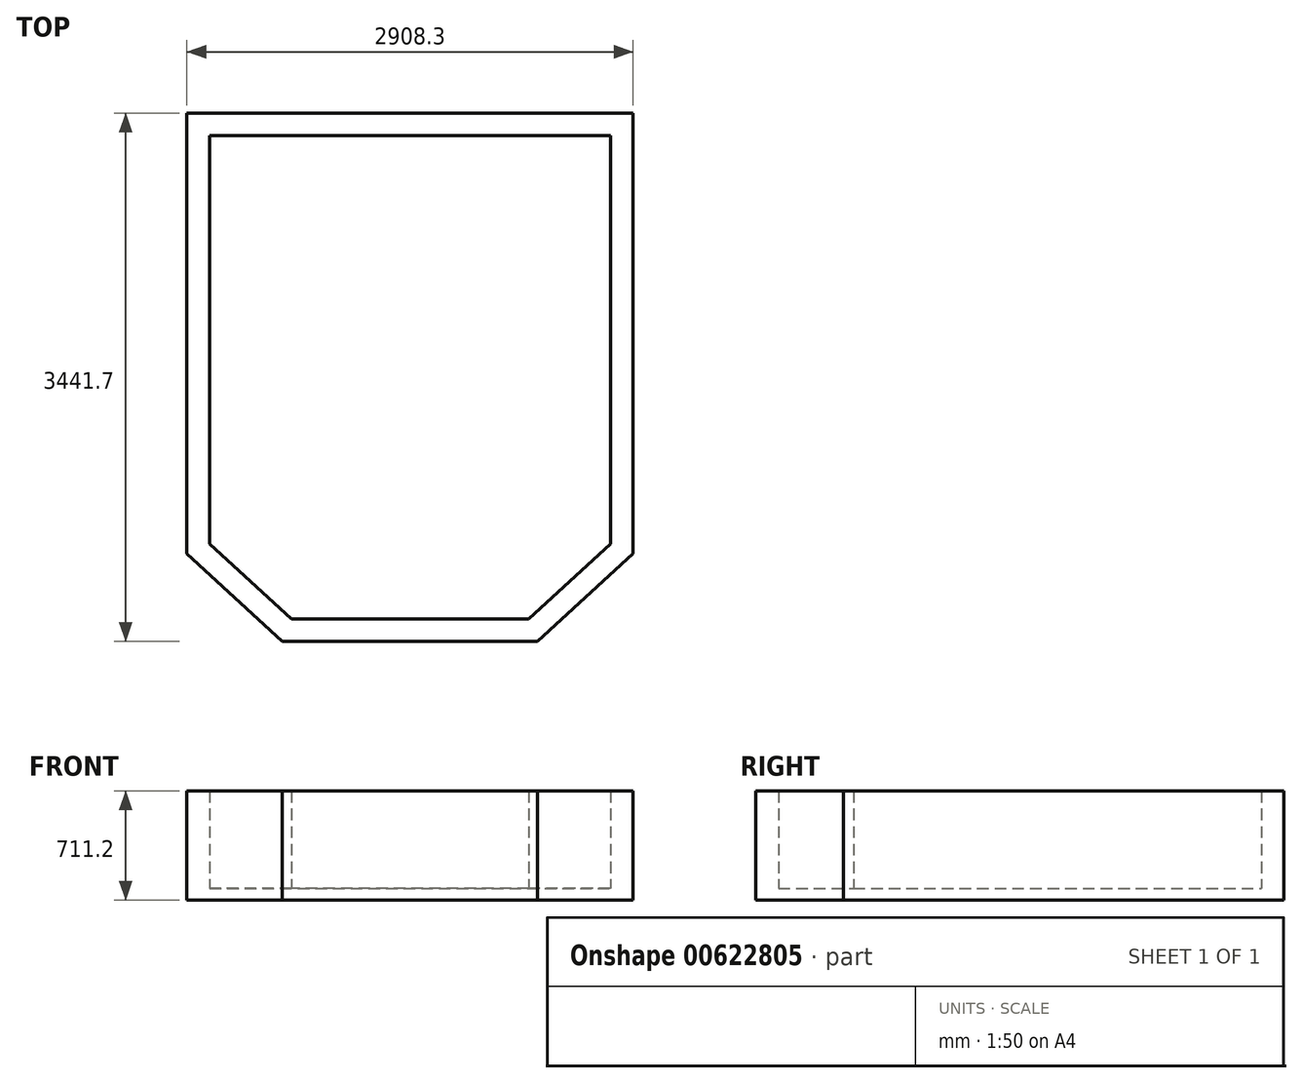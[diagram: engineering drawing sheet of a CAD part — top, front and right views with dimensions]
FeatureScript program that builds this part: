
annotation { "Feature Type Name" : "Feature", "Feature Type Description" : "" }
export const myFeature = defineFeature(function(context is Context, id is Id, definition is map)
    precondition{}
    {
        {
            var Q0;
            Q0=qCreatedBy(makeId("Top.planeOp"),FACE);
            var sketch = newSketch(context, id + "F0", { "sketchPlane" : qUnion([Q0])});
            skLineSegment(sketch, "E0", {"start": v(0, 0) * mm, "end": v(2908.3, 0) * mm});
            skLineSegment(sketch, "E1", {"start": v(2908.3, 0) * mm, "end": v(2908.3, -2870.2) * mm});
            skLineSegment(sketch, "E2", {"start": v(2908.3, -2870.2) * mm, "end": v(2286, -3441.7) * mm});
            skLineSegment(sketch, "E3", {"start": v(2286, -3441.7) * mm, "end": v(622.3, -3441.7) * mm});
            skLineSegment(sketch, "E4", {"start": v(622.3, -3441.7) * mm, "end": v(0, -2870.2) * mm});
            skLineSegment(sketch, "E5", {"start": v(0, -2870.2) * mm, "end": v(0, 0) * mm});
            skLineSegment(sketch, "E6.0", {"start": v(679.68, -3294.38) * mm, "end": v(147.32, -2805.47) * mm});
            skLineSegment(sketch, "E6.1", {"start": v(147.32, -147.32) * mm, "end": v(2760.98, -147.32) * mm});
            skLineSegment(sketch, "E6.2", {"start": v(2760.98, -147.32) * mm, "end": v(2760.98, -2805.47) * mm});
            skLineSegment(sketch, "E6.3", {"start": v(147.32, -2805.47) * mm, "end": v(147.32, -147.32) * mm});
            skLineSegment(sketch, "E6.4", {"start": v(2760.98, -2805.47) * mm, "end": v(2228.62, -3294.38) * mm});
            skLineSegment(sketch, "E6.5", {"start": v(2228.62, -3294.38) * mm, "end": v(679.68, -3294.38) * mm});
            skSolve(sketch);
        }
        {
            var Q0;
            Q0=makeQuery(id+"F0.imprint","IMPRINT",FACE,{"disambiguationData":[TD([[makeQuery(id+"F0.imprint","IMPRINT",EDGE,{"derivedFrom":sQuery(id+"F0.wireOp",EDGE,"E0")}),-1.0]])]});
            var Q1;
            Q1=makeQuery(id+"F0.imprint","IMPRINT",FACE,{"disambiguationData":[TD([[makeQuery(id+"F0.imprint","IMPRINT",EDGE,{"derivedFrom":sQuery(id+"F0.wireOp",EDGE,"E6.0")}),-1.0]])]});
            extrude(context, id + "F1", {"entities" : qUnion([Q0, Q1]), "oppositeDirection" : true, "depth" : 76.2 * mm, "offsetDistance" : 25.4 * mm});
        }
        {
            var Q0;
            Q0=makeQuery(id+"F0.imprint","IMPRINT",FACE,{"disambiguationData":[TD([[makeQuery(id+"F0.imprint","IMPRINT",EDGE,{"derivedFrom":sQuery(id+"F0.wireOp",EDGE,"E0")}),-1.0]])]});
            extrude(context, id + "F2", {"entities" : qUnion([Q0]), "operationType" : NewBodyOperationType.ADD, "depth" : 635 * mm, "offsetDistance" : 25.4 * mm});
        }
    });
